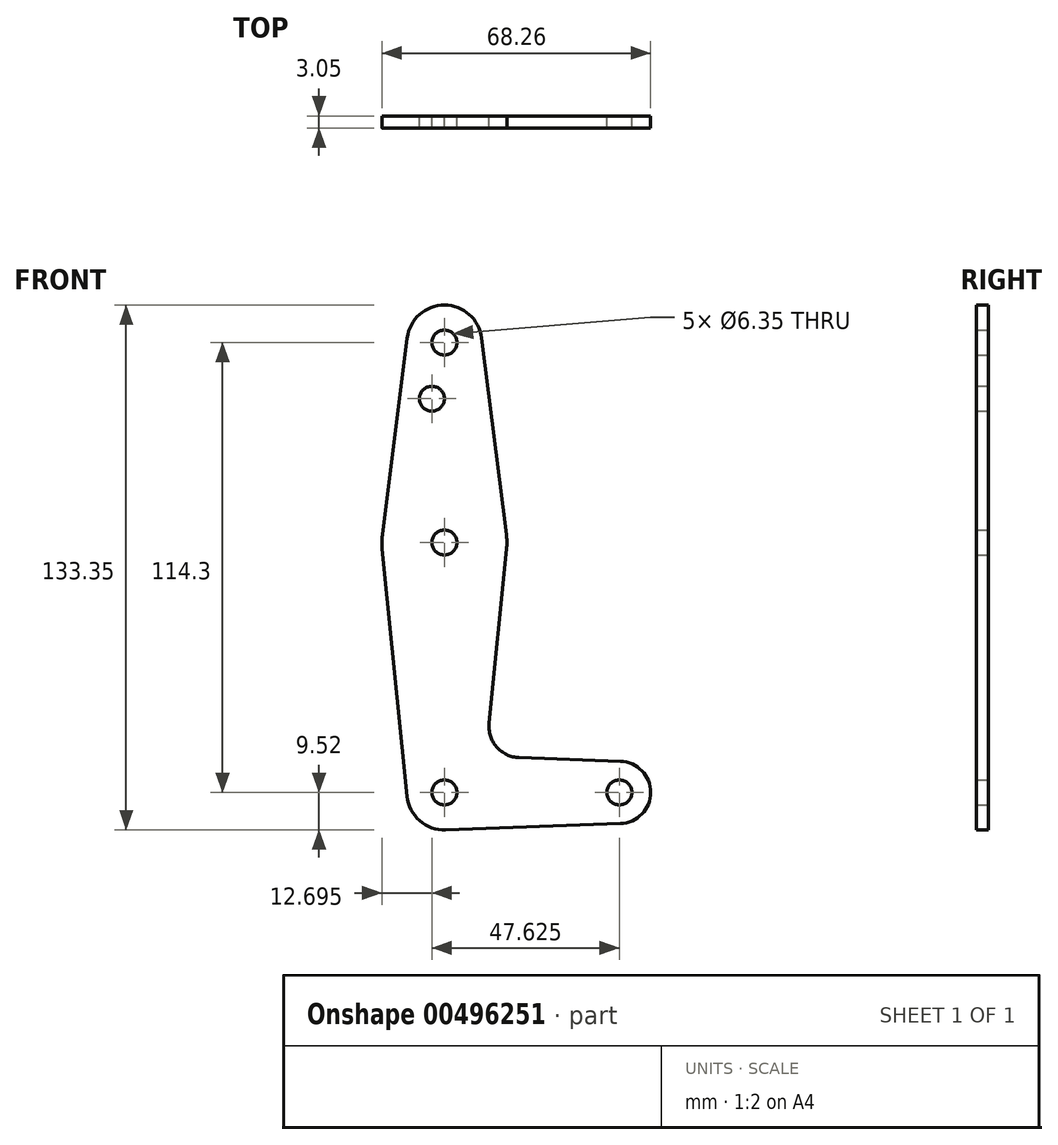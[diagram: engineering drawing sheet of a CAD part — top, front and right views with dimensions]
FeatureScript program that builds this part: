
annotation { "Feature Type Name" : "Feature", "Feature Type Description" : "" }
export const myFeature = defineFeature(function(context is Context, id is Id, definition is map)
    precondition{}
    {
        {
            var Q0;
            Q0=qCreatedBy(makeId("Front.planeOp"),FACE);
            var sketch = newSketch(context, id + "F0", { "sketchPlane" : qUnion([Q0])});
            skLineSegment(sketch, "E0", {"start": v(0, 0) * mm, "end": v(0, 9.53) * mm, "construction": true});
            skLineSegment(sketch, "E1", {"start": v(0, 0) * mm, "end": v(44.45, 0) * mm, "construction": true});
            skCircle(sketch, "E2", {"center": v(0, 0) * mm, "radius": 9.53 * mm});
            skCircle(sketch, "E3", {"center": v(44.45, 0) * mm, "radius": 7.94 * mm});
            skCircle(sketch, "E4", {"center": v(0, 63.5) * mm, "radius": 15.88 * mm});
            skLineSegment(sketch, "E5", {"start": v(0, 0) * mm, "end": v(0, 114.3) * mm, "construction": true});
            skCircle(sketch, "E6", {"center": v(0, 114.3) * mm, "radius": 9.53 * mm});
            skLineSegment(sketch, "E7", {"start": v(-9.45, 115.5) * mm, "end": v(-15.75, 65.48) * mm});
            skLineSegment(sketch, "E8", {"start": v(9.45, 115.5) * mm, "end": v(15.75, 65.48) * mm});
            skLineSegment(sketch, "E9", {"start": v(-15.8, 61.91) * mm, "end": v(-9.48, -0.95) * mm});
            skLineSegment(sketch, "E10", {"start": v(15.8, 61.91) * mm, "end": v(11.34, 17.6) * mm});
            skLineSegment(sketch, "E11", {"start": v(0.34, -9.52) * mm, "end": v(44.73, -7.93) * mm});
            skLineSegment(sketch, "E12", {"start": v(44.73, 7.93) * mm, "end": v(18.97, 8.85) * mm});
            skArc(sketch, "E13.filletArc", {"start": v(11.34, 17.6) * mm, "mid": v(13.26, 11.57) * mm, "end": v(18.97, 8.85) * mm});
            skCircle(sketch, "E14", {"center": v(0, 0) * mm, "radius": 3.18 * mm});
            skCircle(sketch, "E15", {"center": v(44.45, 0) * mm, "radius": 3.18 * mm});
            skCircle(sketch, "E16", {"center": v(0, 63.5) * mm, "radius": 3.18 * mm});
            skCircle(sketch, "E17", {"center": v(0, 114.3) * mm, "radius": 3.18 * mm});
            skCircle(sketch, "E18", {"center": v(-3.18, 100.03) * mm, "radius": 3.18 * mm});
            skSolve(sketch);
        }
        {
            var Q0;
            Q0 = qSketchRegion(id + "F0", true);
            extrude(context, id + "F1", {"entities" : qUnion([Q0]), "depth" : 3.05 * mm});
        }
    });
